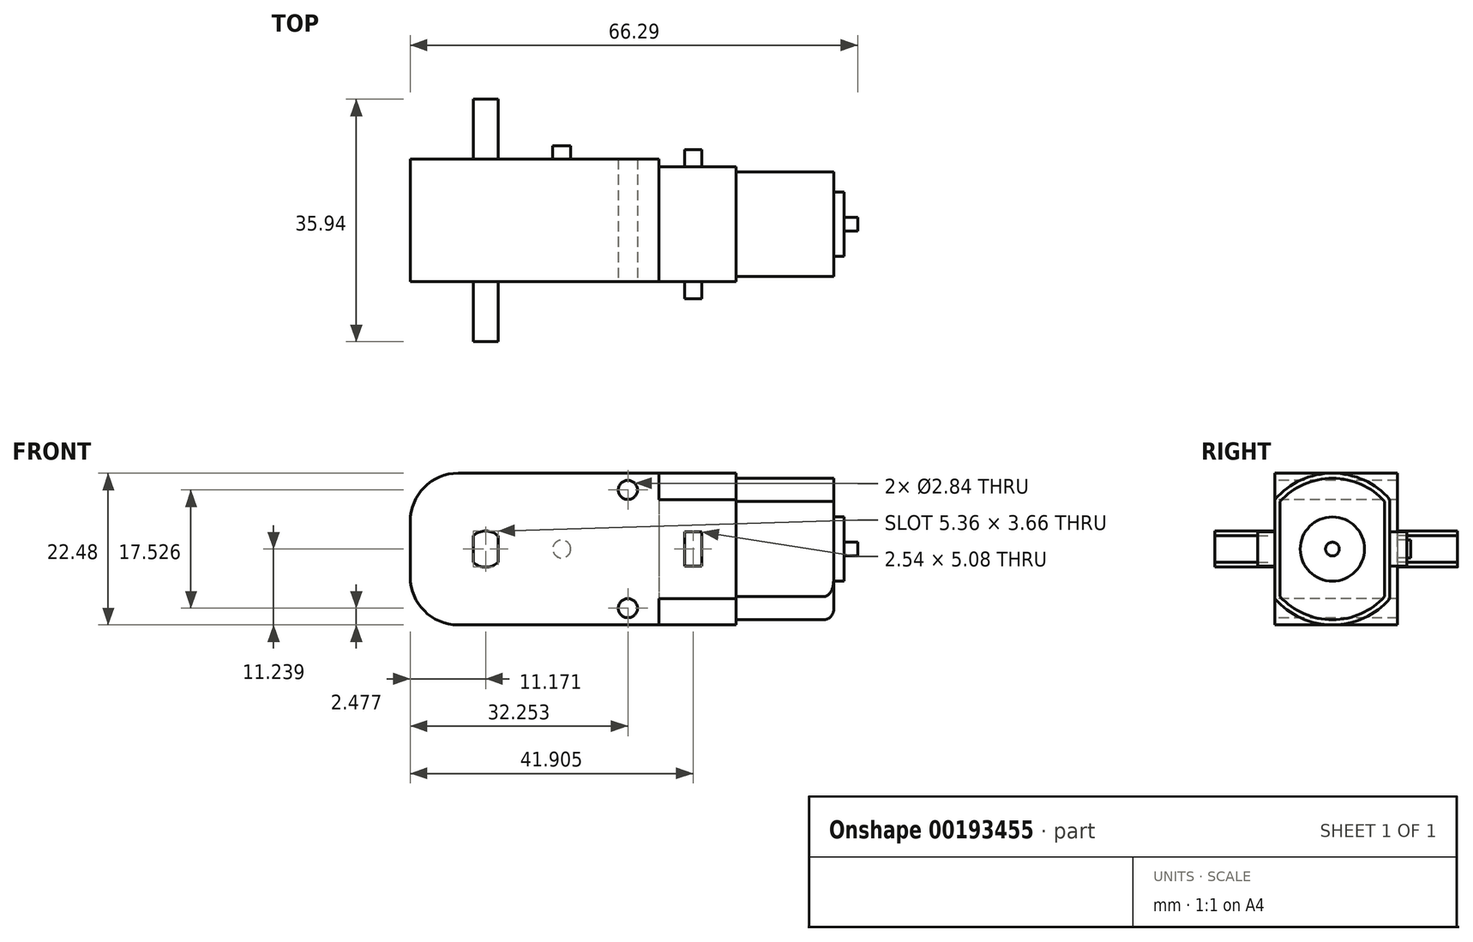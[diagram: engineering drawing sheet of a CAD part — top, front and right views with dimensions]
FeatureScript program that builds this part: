
annotation { "Feature Type Name" : "Feature", "Feature Type Description" : "" }
export const myFeature = defineFeature(function(context is Context, id is Id, definition is map)
    precondition{}
    {
        {
            var Q0;
            Q0=qCreatedBy(makeId("Top.planeOp"),FACE);
            var sketch = newSketch(context, id + "F0", { "sketchPlane" : qUnion([Q0])});
            skLineSegment(sketch, "E0.bottom", {"start": v(49.21, -49.21) * mm, "end": v(-49.21, -49.21) * mm, "construction": true});
            skLineSegment(sketch, "E0.top", {"start": v(49.21, 49.21) * mm, "end": v(-49.21, 49.21) * mm, "construction": true});
            skLineSegment(sketch, "E0.left", {"start": v(49.21, -49.21) * mm, "end": v(49.21, 49.21) * mm, "construction": true});
            skLineSegment(sketch, "E0.right", {"start": v(-49.21, -49.21) * mm, "end": v(-49.21, 49.21) * mm, "construction": true});
            skPoint(sketch, "E0.middle", {"position": v(0, 0) * mm});
            skLineSegment(sketch, "E1", {"start": v(-35.05, -0.76) * mm, "end": v(35.05, -0.76) * mm, "construction": true});
            skLineSegment(sketch, "E2", {"start": v(0, 11.11) * mm, "end": v(0, -11.11) * mm, "construction": true});
            skLineSegment(sketch, "E3", {"start": v(-18.41, 7.75) * mm, "end": v(18.42, 7.75) * mm});
            skLineSegment(sketch, "E4.MirrorCS", {"start": v(-18.41, -9.27) * mm, "end": v(18.41, -9.27) * mm});
            skLineSegment(sketch, "E5", {"start": v(18.42, 7.75) * mm, "end": v(18.42, -9.27) * mm});
            skLineSegment(sketch, "E6.MirrorCS", {"start": v(-18.42, 7.75) * mm, "end": v(-18.41, -9.27) * mm});
            skPoint(sketch, "E7.orphan", {"position": v(12.01, 7.75) * mm});
            skPoint(sketch, "E8.orphan", {"position": v(12.01, -9.27) * mm});
            skPoint(sketch, "E9.orphan", {"position": v(18.42, -26.12) * mm});
            skPoint(sketch, "E10.orphan", {"position": v(-18.41, -26.12) * mm});
            skPoint(sketch, "E11.orphan", {"position": v(-32.46, 7.75) * mm});
            skPoint(sketch, "E12.orphan", {"position": v(-18.42, 15.48) * mm});
            skPoint(sketch, "E13.orphan", {"position": v(18.41, 15.48) * mm});
            skPoint(sketch, "E14.orphan", {"position": v(-32.46, -9.27) * mm});
            skSolve(sketch);
        }
        {
            var Q0;
            Q0=makeQuery(id+"F0.imprint","IMPRINT",FACE,{"disambiguationData":[TD([[makeQuery(id+"F0.imprint","IMPRINT",EDGE,{"derivedFrom":sQuery(id+"F0.wireOp",EDGE,"E3")}),-1.0]])]});
            extrude(context, id + "F1", {"entities" : qUnion([Q0]), "depth" : 22.48 * mm});
        }
        {
            var Q0;
            Q0=makeQuery(id+"F1.opExtrude","CAP_EDGE",EDGE,{"disambiguationData":[OSD([sQuery(id+"F0.wireOp",EDGE,"E6.MirrorCS")])],"isStart":false});
            var Q1;
            Q1=makeQuery(id+"F1.opExtrude","CAP_EDGE",EDGE,{"disambiguationData":[OSD([sQuery(id+"F0.wireOp",EDGE,"E6.MirrorCS")])],"isStart":true});
            fillet(context, id + "F2", {"entities" : qUnion([Q0, Q1]), "radius" : 7.11 * mm, "tangentPropagation" : true, "allowEdgeOverflow" : false});
        }
        {
            var Q0;
            Q0=makeQuery(id+"F1.opExtrude","SWEPT_FACE",FACE,{"disambiguationData":[OSD([sQuery(id+"F0.wireOp",EDGE,"E5")])]});
            var sketch = newSketch(context, id + "F3", { "sketchPlane" : qUnion([Q0])});
            skLineSegment(sketch, "E15", {"start": v(-9.27, 11.24) * mm, "end": v(7.75, 11.24) * mm, "construction": true});
            skArc(sketch, "E16", {"start": v(-9.27, 3.9) * mm, "mid": v(-0.76, 0) * mm, "end": v(7.75, 3.9) * mm});
            skLineSegment(sketch, "E17.0", {"start": v(-9.27, 18.58) * mm, "end": v(-9.27, 3.9) * mm});
            skLineSegment(sketch, "E18.0", {"start": v(7.75, 18.58) * mm, "end": v(7.75, 3.9) * mm});
            skPoint(sketch, "E19.orphan", {"position": v(-9.27, 22.48) * mm});
            skPoint(sketch, "E20.orphan", {"position": v(7.75, 22.48) * mm});
            skArc(sketch, "E21.trimOffspring", {"start": v(7.75, 18.58) * mm, "mid": v(-0.76, 22.48) * mm, "end": v(-9.27, 18.58) * mm});
            skPoint(sketch, "E22.orphan", {"position": v(7.75, 0) * mm});
            skPoint(sketch, "E23.orphan", {"position": v(-9.27, 0) * mm});
            skSolve(sketch);
        }
        {
            var Q0;
            {var subQ1=sQuery(id+"F3.wireOp",EDGE,"E17.0");Q0=makeQuery(id+"F3.imprint","IMPRINT",FACE,{"disambiguationData":[TD([[makeQuery(id+"F3.imprint","IMPRINT",EDGE,{"derivedFrom":subQ1}),1.0]])]});}
            var Q1;
            Q1=makeQuery(id+"F1.opExtrude","SWEPT_FACE",FACE,{"disambiguationData":[OSD([sQuery(id+"F0.wireOp",EDGE,"E6.MirrorCS")])]});
            extrude(context, id + "F4", {"entities" : qUnion([Q0, Q1]), "operationType" : NewBodyOperationType.ADD, "depth" : 27.43 * mm});
        }
        {
            var Q0;
            Q0=makeQuery(id+"F4.opExtrude","CAP_FACE",FACE,{"disambiguationData":[OSD([sQuery(id+"F3.wireOp",EDGE,"E16"),sQuery(id+"F3.wireOp",EDGE,"E17.0"),sQuery(id+"F3.wireOp",EDGE,"E18.0"),sQuery(id+"F3.wireOp",EDGE,"E21.trimOffspring")])],"isStart":false});
            var sketch = newSketch(context, id + "F5", { "sketchPlane" : qUnion([Q0])});
            skLineSegment(sketch, "E24.0", {"start": v(-8.5, 18.3) * mm, "end": v(-8.5, 4.19) * mm});
            skArc(sketch, "E24.1", {"start": v(6.99, 18.3) * mm, "mid": v(-0.76, 21.72) * mm, "end": v(-8.5, 18.3) * mm});
            skLineSegment(sketch, "E24.2", {"start": v(6.99, 4.19) * mm, "end": v(6.99, 18.3) * mm});
            skArc(sketch, "E24.3", {"start": v(-8.5, 4.19) * mm, "mid": v(-0.76, 0.76) * mm, "end": v(6.99, 4.19) * mm});
            skLineSegment(sketch, "E25.0", {"start": v(-14.86, 20.43) * mm, "end": v(-14.86, 2.05) * mm});
            skArc(sketch, "E25.1", {"start": v(13.34, 20.43) * mm, "mid": v(-0.76, 28.07) * mm, "end": v(-14.86, 20.43) * mm});
            skLineSegment(sketch, "E25.2", {"start": v(13.34, 2.05) * mm, "end": v(13.34, 20.43) * mm});
            skArc(sketch, "E25.3", {"start": v(-14.86, 2.05) * mm, "mid": v(-0.76, -5.59) * mm, "end": v(13.34, 2.05) * mm});
            skSolve(sketch);
        }
        {
            var Q0;
            Q0=makeQuery(id+"F5.imprint","IMPRINT",FACE,{"disambiguationData":[TD([[makeQuery(id+"F5.imprint","IMPRINT",EDGE,{"derivedFrom":sQuery(id+"F5.wireOp",EDGE,"E25.0")}),1.0]])]});
            var Q1;
            Q1=makeQuery(id+"F5.imprint","IMPRINT",FACE,{"disambiguationData":[TD([[makeQuery(id+"F5.imprint","IMPRINT",EDGE,{"derivedFrom":sQuery(id+"F5.wireOp",EDGE,"E24.0")}),-1.0]])]});
            extrude(context, id + "F6", {"entities" : qUnion([Q0, Q1]), "operationType" : NewBodyOperationType.REMOVE, "oppositeDirection" : true, "depth" : 16 * mm});
        }
        {
            var Q0;
            Q0=makeQuery(id+"F4.opExtrude","CAP_FACE",FACE,{"disambiguationData":[OSD([sQuery(id+"F3.wireOp",EDGE,"E16"),sQuery(id+"F3.wireOp",EDGE,"E17.0"),sQuery(id+"F3.wireOp",EDGE,"E18.0"),sQuery(id+"F3.wireOp",EDGE,"E21.trimOffspring")])],"isStart":false});
            var sketch = newSketch(context, id + "F7", { "sketchPlane" : qUnion([Q0])});
            skCircle(sketch, "E26", {"center": v(-0.76, 11.24) * mm, "radius": 4.76 * mm});
            skCircle(sketch, "E27", {"center": v(-0.76, 11.24) * mm, "radius": 12.82 * mm});
            skSolve(sketch);
        }
        {
            var Q0;
            Q0=makeQuery(id+"F7.imprint","IMPRINT",FACE,{"disambiguationData":[TD([[makeQuery(id+"F7.imprint","IMPRINT",EDGE,{"derivedFrom":sQuery(id+"F7.wireOp",EDGE,"E27")}),1.0]])]});
            var Q1;
            Q1=makeQuery(id+"F7.imprint","IMPRINT",FACE,{"disambiguationData":[TD([[makeQuery(id+"F7.imprint","IMPRINT",EDGE,{"derivedFrom":sQuery(id+"F7.wireOp",EDGE,"E26")}),-1.0]])]});
            extrude(context, id + "F8", {"entities" : qUnion([Q0, Q1]), "operationType" : NewBodyOperationType.REMOVE, "oppositeDirection" : true, "depth" : 1.52 * mm});
        }
        {
            var Q0;
            Q0=makeQuery(id+"F8.boolean.opBoolean","INTERSECT",EDGE,{"derivedFrom":[makeQuery(id+"F6.boolean.opBoolean","COPY",FACE,{"derivedFrom":makeQuery(id+"F6.opExtrude","SWEPT_FACE",FACE,{"disambiguationData":[OSD([sQuery(id+"F5.wireOp",EDGE,"E24.3")])]})}),makeQuery(id+"F8.opExtrude","CAP_FACE",FACE,{"disambiguationData":[OSD([sQuery(id+"F7.wireOp",EDGE,"E26"),sQuery(id+"F7.wireOp",EDGE,"E27")])],"isStart":false})]});
            fillet(context, id + "F9", {"entities" : qUnion([Q0]), "radius" : 1.52 * mm, "tangentPropagation" : true, "allowEdgeOverflow" : false});
        }
        {
            var Q0;
            Q0=makeQuery(id+"F4.opExtrude","CAP_FACE",FACE,{"disambiguationData":[OSD([sQuery(id+"F3.wireOp",EDGE,"E16"),sQuery(id+"F3.wireOp",EDGE,"E17.0"),sQuery(id+"F3.wireOp",EDGE,"E18.0"),sQuery(id+"F3.wireOp",EDGE,"E21.trimOffspring")])],"isStart":false});
            var sketch = newSketch(context, id + "F10", { "sketchPlane" : qUnion([Q0])});
            skCircle(sketch, "E28", {"center": v(-0.76, 11.24) * mm, "radius": 1.02 * mm});
            skSolve(sketch);
        }
        {
            var Q0;
            Q0=makeQuery(id+"F10.imprint","IMPRINT",FACE,{"disambiguationData":[TD([[makeQuery(id+"F10.imprint","IMPRINT",EDGE,{"derivedFrom":sQuery(id+"F10.wireOp",EDGE,"E28")}),1.0]])]});
            extrude(context, id + "F11", {"entities" : qUnion([Q0]), "operationType" : NewBodyOperationType.ADD, "depth" : 2.03 * mm});
        }
        {
            var Q0;
            Q0=makeQuery(id+"F4.boolean.opBoolean","MERGE",FACE,{"derivedFrom":[makeQuery(id+"F1.opExtrude","SWEPT_FACE",FACE,{"disambiguationData":[OSD([sQuery(id+"F0.wireOp",EDGE,"E4.MirrorCS")])]}),makeQuery(id+"F4.opExtrude","SWEPT_FACE",FACE,{"disambiguationData":[OSD([sQuery(id+"F3.wireOp",EDGE,"E17.0")])]})]});
            var sketch = newSketch(context, id + "F12", { "sketchPlane" : qUnion([Q0])});
            skLineSegment(sketch, "E29", {"start": v(29.85, 11.24) * mm, "end": v(18.51, 11.24) * mm, "construction": true});
            skLineSegment(sketch, "E30", {"start": v(22.23, 13.78) * mm, "end": v(22.23, 8.7) * mm});
            skLineSegment(sketch, "E31", {"start": v(24.77, 13.78) * mm, "end": v(24.77, 8.7) * mm});
            skLineSegment(sketch, "E32", {"start": v(22.23, 13.78) * mm, "end": v(24.77, 13.78) * mm});
            skLineSegment(sketch, "E33.MirrorCS", {"start": v(22.23, 8.7) * mm, "end": v(24.77, 8.7) * mm});
            skPoint(sketch, "E34.orphan", {"position": v(19.69, 8.7) * mm});
            skPoint(sketch, "E35.orphan", {"position": v(27.19, 8.7) * mm});
            skPoint(sketch, "E36.orphan", {"position": v(27.19, 13.78) * mm});
            skPoint(sketch, "E37.orphan", {"position": v(19.69, 13.78) * mm});
            skSolve(sketch);
        }
        {
            var Q0;
            Q0=makeQuery(id+"F12.imprint","IMPRINT",FACE,{"disambiguationData":[TD([[makeQuery(id+"F12.imprint","IMPRINT",EDGE,{"derivedFrom":sQuery(id+"F12.wireOp",EDGE,"E30")}),1.0]])]});
            extrude(context, id + "F13", {"entities" : qUnion([Q0]), "operationType" : NewBodyOperationType.ADD, "depth" : 2.54 * mm});
        }
        {
            var Q0;
            Q0=makeQuery(id+"F4.boolean.opBoolean","MERGE",FACE,{"derivedFrom":[makeQuery(id+"F1.opExtrude","SWEPT_FACE",FACE,{"disambiguationData":[OSD([sQuery(id+"F0.wireOp",EDGE,"E3")])]}),makeQuery(id+"F4.opExtrude","SWEPT_FACE",FACE,{"disambiguationData":[OSD([sQuery(id+"F3.wireOp",EDGE,"E18.0")])]})]});
            var sketch = newSketch(context, id + "F14", { "sketchPlane" : qUnion([Q0])});
            skLineSegment(sketch, "E38.0", {"start": v(11.3, 0) * mm, "end": v(-18.42, 0) * mm});
            skArc(sketch, "E39.0", {"start": v(11.3, 0) * mm, "mid": v(16.33, 2.08) * mm, "end": v(18.41, 7.11) * mm});
            skLineSegment(sketch, "E40.0", {"start": v(18.42, 15.37) * mm, "end": v(18.42, 7.11) * mm});
            skArc(sketch, "E41.0", {"start": v(18.41, 15.37) * mm, "mid": v(16.33, 20.4) * mm, "end": v(11.3, 22.48) * mm});
            skLineSegment(sketch, "E42.0", {"start": v(11.3, 22.48) * mm, "end": v(-18.42, 22.48) * mm});
            skLineSegment(sketch, "E43", {"start": v(-18.42, 22.48) * mm, "end": v(-18.42, 0) * mm});
            skSolve(sketch);
        }
        {
            var Q0;
            {var subQ0=sQuery(id+"F14.wireOp",EDGE,"E38.0");Q0=makeQuery(id+"F14.imprint","IMPRINT",FACE,{"disambiguationData":[TD([[makeQuery(id+"F14.imprint","IMPRINT",EDGE,{"derivedFrom":subQ0}),-1.0]])]});}
            extrude(context, id + "F15", {"entities" : qUnion([Q0]), "operationType" : NewBodyOperationType.ADD, "depth" : 1.14 * mm});
        }
        {
            var Q0;
            Q0=makeQuery(id+"F4.boolean.opBoolean","MERGE",FACE,{"derivedFrom":[makeQuery(id+"F1.opExtrude","SWEPT_FACE",FACE,{"disambiguationData":[OSD([sQuery(id+"F0.wireOp",EDGE,"E3")])]}),makeQuery(id+"F4.opExtrude","SWEPT_FACE",FACE,{"disambiguationData":[OSD([sQuery(id+"F3.wireOp",EDGE,"E18.0")])]})]});
            var sketch = newSketch(context, id + "F16", { "sketchPlane" : qUnion([Q0])});
            skLineSegment(sketch, "E44.0.0", {"start": v(-24.77, 13.78) * mm, "end": v(-22.23, 13.78) * mm});
            skLineSegment(sketch, "E44.0.1", {"start": v(-22.23, 13.78) * mm, "end": v(-22.23, 8.7) * mm});
            skLineSegment(sketch, "E44.0.2", {"start": v(-22.23, 8.7) * mm, "end": v(-24.77, 8.7) * mm});
            skLineSegment(sketch, "E44.0.3", {"start": v(-24.77, 8.7) * mm, "end": v(-24.77, 13.78) * mm});
            skSolve(sketch);
        }
        {
            var Q0;
            Q0=makeQuery(id+"F16.imprint","IMPRINT",FACE,{"disambiguationData":[TD([[makeQuery(id+"F16.imprint","IMPRINT",EDGE,{"derivedFrom":sQuery(id+"F16.wireOp",EDGE,"E44.0.0")}),-1.0]])]});
            extrude(context, id + "F17", {"entities" : qUnion([Q0]), "operationType" : NewBodyOperationType.ADD, "depth" : 2.54 * mm});
        }
        {
            var Q0;
            Q0=makeQuery(id+"F4.boolean.opBoolean","MERGE",FACE,{"derivedFrom":[makeQuery(id+"F1.opExtrude","SWEPT_FACE",FACE,{"disambiguationData":[OSD([sQuery(id+"F0.wireOp",EDGE,"E4.MirrorCS")])]}),makeQuery(id+"F4.opExtrude","SWEPT_FACE",FACE,{"disambiguationData":[OSD([sQuery(id+"F3.wireOp",EDGE,"E17.0")])]})]});
            var sketch = newSketch(context, id + "F18", { "sketchPlane" : qUnion([Q0])});
            skArc(sketch, "E45", {"start": v(-5.41, 13.2) * mm, "mid": v(-7.24, 13.92) * mm, "end": v(-9.07, 13.2) * mm});
            skPoint(sketch, "E45.centerSnap0", {"position": v(-18.41, 11.24) * mm});
            skLineSegment(sketch, "E46", {"start": v(-9.07, 13.2) * mm, "end": v(-9.07, 9.28) * mm});
            skLineSegment(sketch, "E47", {"start": v(-5.41, 13.2) * mm, "end": v(-5.41, 9.28) * mm});
            skPoint(sketch, "E48.orphan", {"position": v(-9.07, 5.55) * mm});
            skArc(sketch, "E49.trimOffspring", {"start": v(-9.07, 9.28) * mm, "mid": v(-7.24, 8.56) * mm, "end": v(-5.41, 9.28) * mm});
            skSolve(sketch);
        }
        {
            var Q0;
            Q0=makeQuery(id+"F18.imprint","IMPRINT",FACE,{"disambiguationData":[TD([[makeQuery(id+"F18.imprint","IMPRINT",EDGE,{"derivedFrom":sQuery(id+"F18.wireOp",EDGE,"E45")}),1.0]])]});
            extrude(context, id + "F19", {"entities" : qUnion([Q0]), "operationType" : NewBodyOperationType.ADD, "depth" : 8.9 * mm});
        }
        {
            var Q0;
            Q0=makeQuery(id+"F15.opExtrude","CAP_FACE",FACE,{"disambiguationData":[OSD([sQuery(id+"F14.wireOp",EDGE,"E38.0"),sQuery(id+"F14.wireOp",EDGE,"E39.0"),sQuery(id+"F14.wireOp",EDGE,"E40.0"),sQuery(id+"F14.wireOp",EDGE,"E41.0"),sQuery(id+"F14.wireOp",EDGE,"E42.0"),sQuery(id+"F14.wireOp",EDGE,"E43")])],"isStart":false});
            var sketch = newSketch(context, id + "F20", { "sketchPlane" : qUnion([Q0])});
            skLineSegment(sketch, "E50.0.0", {"start": v(5.41, 9.28) * mm, "end": v(5.41, 13.2) * mm});
            skArc(sketch, "E50.0.1", {"start": v(5.41, 13.2) * mm, "mid": v(7.24, 13.92) * mm, "end": v(9.07, 13.2) * mm});
            skLineSegment(sketch, "E50.0.2", {"start": v(9.07, 13.2) * mm, "end": v(9.07, 9.28) * mm});
            skArc(sketch, "E50.0.3", {"start": v(9.07, 9.28) * mm, "mid": v(7.24, 8.56) * mm, "end": v(5.41, 9.28) * mm});
            skSolve(sketch);
        }
        {
            var Q0;
            Q0=makeQuery(id+"F20.imprint","IMPRINT",FACE,{"disambiguationData":[TD([[makeQuery(id+"F20.imprint","IMPRINT",EDGE,{"derivedFrom":sQuery(id+"F20.wireOp",EDGE,"E50.0.0")}),-1.0]])]});
            extrude(context, id + "F21", {"entities" : qUnion([Q0]), "operationType" : NewBodyOperationType.ADD, "depth" : 8.9 * mm});
        }
        {
            var Q0;
            Q0=makeQuery(id+"F15.opExtrude","CAP_FACE",FACE,{"disambiguationData":[OSD([sQuery(id+"F14.wireOp",EDGE,"E38.0"),sQuery(id+"F14.wireOp",EDGE,"E39.0"),sQuery(id+"F14.wireOp",EDGE,"E40.0"),sQuery(id+"F14.wireOp",EDGE,"E41.0"),sQuery(id+"F14.wireOp",EDGE,"E42.0"),sQuery(id+"F14.wireOp",EDGE,"E43")])],"isStart":false});
            var sketch = newSketch(context, id + "F22", { "sketchPlane" : qUnion([Q0])});
            skLineSegment(sketch, "E51", {"start": v(7.24, 13.92) * mm, "end": v(7.24, 8.56) * mm, "construction": true});
            skLineSegment(sketch, "E52", {"start": v(-4.04, 11.24) * mm, "end": v(-4.04, 17.91) * mm, "construction": true});
            skLineSegment(sketch, "E53", {"start": v(18.42, 11.24) * mm, "end": v(0, 11.24) * mm, "construction": true});
            skCircle(sketch, "E54", {"center": v(-4.04, 11.24) * mm, "radius": 1.32 * mm});
            skSolve(sketch);
        }
        {
            var Q0;
            Q0=makeQuery(id+"F22.imprint","IMPRINT",FACE,{"disambiguationData":[TD([[makeQuery(id+"F22.imprint","IMPRINT",EDGE,{"derivedFrom":sQuery(id+"F22.wireOp",EDGE,"E54")}),1.0]])]});
            extrude(context, id + "F23", {"entities" : qUnion([Q0]), "operationType" : NewBodyOperationType.ADD, "depth" : 1.96 * mm});
        }
        {
            var Q0;
            Q0=makeQuery(id+"F4.boolean.opBoolean","MERGE",FACE,{"derivedFrom":[makeQuery(id+"F1.opExtrude","SWEPT_FACE",FACE,{"disambiguationData":[OSD([sQuery(id+"F0.wireOp",EDGE,"E4.MirrorCS")])]}),makeQuery(id+"F4.opExtrude","SWEPT_FACE",FACE,{"disambiguationData":[OSD([sQuery(id+"F3.wireOp",EDGE,"E17.0")])]})]});
            var sketch = newSketch(context, id + "F24", { "sketchPlane" : qUnion([Q0])});
            skCircle(sketch, "E55", {"center": v(13.84, 20) * mm, "radius": 1.42 * mm});
            skLineSegment(sketch, "E56", {"start": v(-5.41, 11.24) * mm, "end": v(15.76, 11.24) * mm, "construction": true});
            skCircle(sketch, "E57.MirrorC", {"center": v(13.84, 2.48) * mm, "radius": 1.42 * mm});
            skSolve(sketch);
        }
        {
            var Q0;
            Q0 = qSketchRegion(id + "F24", true);
            extrude(context, id + "F25", {"entities" : qUnion([Q0]), "operationType" : NewBodyOperationType.REMOVE, "oppositeDirection" : true, "depth" : 25.4 * mm});
        }
    });
